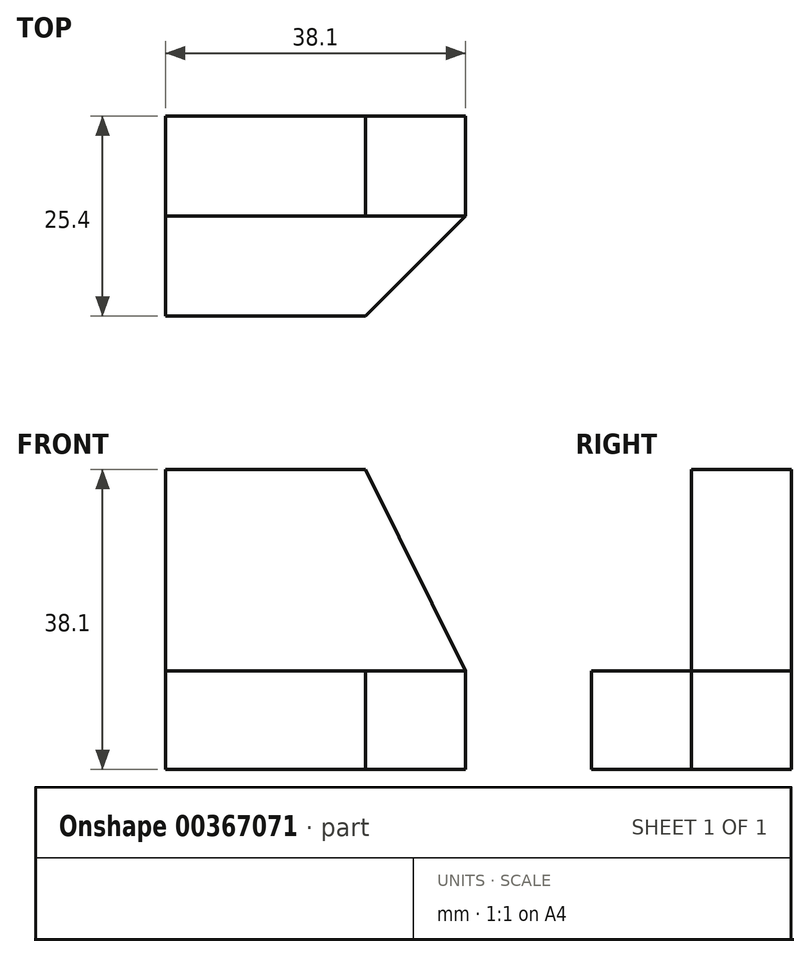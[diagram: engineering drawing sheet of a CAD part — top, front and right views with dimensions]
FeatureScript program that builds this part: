
annotation { "Feature Type Name" : "Feature", "Feature Type Description" : "" }
export const myFeature = defineFeature(function(context is Context, id is Id, definition is map)
    precondition{}
    {
        {
            var Q0;
            Q0=qCreatedBy(makeId("Right.planeOp"),FACE);
            var sketch = newSketch(context, id + "F0", { "sketchPlane" : qUnion([Q0])});
            skLineSegment(sketch, "E0", {"start": v(0, 12.48) * mm, "end": v(12.7, 12.48) * mm});
            skLineSegment(sketch, "E1", {"start": v(12.7, 12.48) * mm, "end": v(12.7, 38.1) * mm});
            skLineSegment(sketch, "E2", {"start": v(12.7, 38.1) * mm, "end": v(25.4, 38.1) * mm});
            skLineSegment(sketch, "E3", {"start": v(25.4, 38.1) * mm, "end": v(25.4, 0) * mm});
            skLineSegment(sketch, "E4", {"start": v(0, 0) * mm, "end": v(0, 12.48) * mm});
            skLineSegment(sketch, "E5", {"start": v(0, 0) * mm, "end": v(25.4, 0) * mm});
            skSolve(sketch);
        }
        {
            var Q0;
            Q0 = qSketchRegion(id + "F0", true);
            extrude(context, id + "F1", {"entities" : qUnion([Q0]), "depth" : 38.1 * mm});
        }
        {
            var Q0;
            Q0=makeQuery(id+"F1.opExtrude","SWEPT_FACE",FACE,{"disambiguationData":[OSD([sQuery(id+"F0.wireOp",EDGE,"E1")])]});
            var sketch = newSketch(context, id + "F2", { "sketchPlane" : qUnion([Q0])});
            skLineSegment(sketch, "E6", {"start": v(25.4, 38.1) * mm, "end": v(38.1, 12.48) * mm});
            skSolve(sketch);
        }
        {
            var Q0;
            Q0 = qSketchRegion(id + "F2", true);
            var Q1;
            {var subQ0=sQuery(id+"F2.wireOp",EDGE,"E6");Q1=makeQuery(id+"F2.imprint","IMPRINT",FACE,{"disambiguationData":[TD([[makeQuery(id+"F2.imprint","IMPRINT",EDGE,{"derivedFrom":subQ0}),1.0]])]});}
            extrude(context, id + "F3", {"entities" : qUnion([Q0, Q1]), "operationType" : NewBodyOperationType.REMOVE, "oppositeDirection" : true, "depth" : 25.4 * mm});
        }
        {
            var Q0;
            Q0=makeQuery(id+"F1.opExtrude","SWEPT_FACE",FACE,{"disambiguationData":[OSD([sQuery(id+"F0.wireOp",EDGE,"E0")])]});
            var sketch = newSketch(context, id + "F4", { "sketchPlane" : qUnion([Q0])});
            skLineSegment(sketch, "E7", {"start": v(38.1, 12.7) * mm, "end": v(25.4, 0) * mm});
            skSolve(sketch);
        }
        {
            var Q0;
            {var subQ0=sQuery(id+"F4.wireOp",EDGE,"E7");Q0=makeQuery(id+"F4.imprint","IMPRINT",FACE,{"disambiguationData":[TD([[makeQuery(id+"F4.imprint","IMPRINT",EDGE,{"derivedFrom":subQ0}),1.0]])]});}
            extrude(context, id + "F5", {"entities" : qUnion([Q0]), "operationType" : NewBodyOperationType.REMOVE, "oppositeDirection" : true, "depth" : 25.4 * mm});
        }
    });
